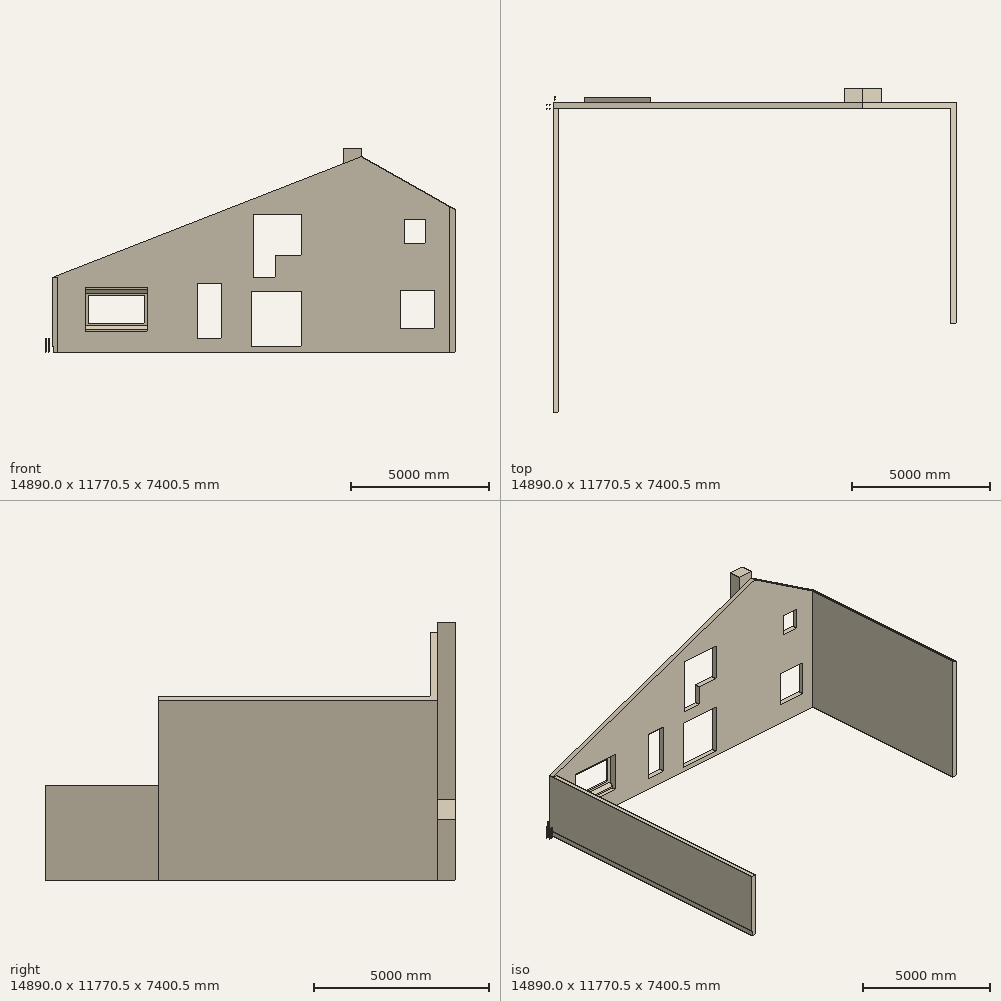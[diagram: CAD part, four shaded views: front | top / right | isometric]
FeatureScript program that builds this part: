
annotation { "Feature Type Name" : "Feature", "Feature Type Description" : "" }
export const myFeature = defineFeature(function(context is Context, id is Id, definition is map)
    precondition{}
    {
        {
            var Q0;
            Q0=qCreatedBy(makeId("Top.planeOp"),FACE);
            var sketch = newSketch(context, id + "F0", { "sketchPlane" : qUnion([Q0])});
            skLineSegment(sketch, "E0", {"start": v(-6130, 0) * mm, "end": v(8510, 0) * mm});
            skLineSegment(sketch, "E1", {"start": v(8510, 0) * mm, "end": v(8510, -8000.5) * mm});
            skLineSegment(sketch, "E2", {"start": v(-6130, 0) * mm, "end": v(-6130, -11250.5) * mm});
            skLineSegment(sketch, "E3.0", {"start": v(8310, -200) * mm, "end": v(8310, -8000.5) * mm});
            skLineSegment(sketch, "E3.1", {"start": v(-5930, -200) * mm, "end": v(8310, -200) * mm});
            skLineSegment(sketch, "E3.2", {"start": v(-5930, -200) * mm, "end": v(-5930, -11250.5) * mm});
            skLineSegment(sketch, "E4", {"start": v(-6130, -11250.5) * mm, "end": v(-5930, -11250.5) * mm});
            skLineSegment(sketch, "E5", {"start": v(8510, -8000.5) * mm, "end": v(8310, -8000.5) * mm});
            skSolve(sketch);
        }
        {
            var Q0;
            Q0 = qSketchRegion(id + "F0", true);
            extrude(context, id + "F1", {"entities" : qUnion([Q0]), "depth" : ((2374.5 - 100) - 50) * mm, "offsetDistance" : 25 * mm, "hasSecondDirection" : true, "secondDirectionOppositeDirection" : true, "secondDirectionDepth" : 490 * mm});
        }
        {
            var Q0;
            Q0=makeQuery(id+"F1.opExtrude","SWEPT_FACE",FACE,{"disambiguationData":[OSD([sQuery(id+"F0.wireOp",EDGE,"E0")])]});
            var sketch = newSketch(context, id + "F2", { "sketchPlane" : qUnion([Q0])});
            skLineSegment(sketch, "E6.bottom", {"start": v(0, 0) * mm, "end": v(850.5, 0) * mm});
            skLineSegment(sketch, "E6.top", {"start": v(0, 2000.5) * mm, "end": v(850.5, 2000.5) * mm});
            skLineSegment(sketch, "E6.left", {"start": v(0, 0) * mm, "end": v(0, 2000.5) * mm});
            skLineSegment(sketch, "E6.right", {"start": v(850.5, 0) * mm, "end": v(850.5, 2000.5) * mm});
            skLineSegment(sketch, "E7.bottom", {"start": v(-1100, -290) * mm, "end": v(-2920, -290) * mm});
            skLineSegment(sketch, "E7.top", {"start": v(-1100, 1710.5) * mm, "end": v(-2920, 1710.5) * mm});
            skLineSegment(sketch, "E7.left", {"start": v(-1100, -290) * mm, "end": v(-1100, 1710.5) * mm});
            skLineSegment(sketch, "E7.right", {"start": v(-2920, -290) * mm, "end": v(-2920, 1710.5) * mm});
            skLineSegment(sketch, "E8.bottom", {"start": v(-6530, 360) * mm, "end": v(-7750, 360) * mm});
            skLineSegment(sketch, "E8.top", {"start": v(-6530, 1760) * mm, "end": v(-7750, 1760) * mm});
            skLineSegment(sketch, "E8.left", {"start": v(-6530, 360) * mm, "end": v(-6530, 1760) * mm});
            skLineSegment(sketch, "E8.right", {"start": v(-7750, 360) * mm, "end": v(-7750, 1760) * mm});
            skLineSegment(sketch, "E9.bottom", {"start": v(-7419.5, 3475.5) * mm, "end": v(-6669.5, 3475.5) * mm});
            skLineSegment(sketch, "E9.top", {"start": v(-7419.5, 4325.5) * mm, "end": v(-6669.5, 4325.5) * mm});
            skLineSegment(sketch, "E9.left", {"start": v(-7419.5, 3475.5) * mm, "end": v(-7419.5, 4325.5) * mm});
            skLineSegment(sketch, "E9.right", {"start": v(-6669.5, 3475.5) * mm, "end": v(-6669.5, 4325.5) * mm});
            skSolve(sketch);
        }
        {
            var Q0;
            Q0=makeQuery(id+"F2.imprint","IMPRINT",FACE,{"disambiguationData":[TD([[makeQuery(id+"F2.imprint","IMPRINT",EDGE,{"derivedFrom":sQuery(id+"F2.wireOp",EDGE,"E6.bottom")}),1.0]])]});
            var Q1;
            Q1=makeQuery(id+"F2.imprint","IMPRINT",FACE,{"disambiguationData":[TD([[makeQuery(id+"F2.imprint","IMPRINT",EDGE,{"derivedFrom":sQuery(id+"F2.wireOp",EDGE,"E7.bottom")}),-1.0]])]});
            var Q2;
            Q2=makeQuery(id+"F2.imprint","IMPRINT",FACE,{"disambiguationData":[TD([[makeQuery(id+"F2.imprint","IMPRINT",EDGE,{"derivedFrom":sQuery(id+"F2.wireOp",EDGE,"E8.bottom")}),-1.0]])]});
            extrude(context, id + "F3", {"entities" : qUnion([Q0, Q1, Q2]), "operationType" : NewBodyOperationType.REMOVE, "endBound" : BoundingType.UP_TO_NEXT, "oppositeDirection" : true, "depth" : 25 * mm, "offsetDistance" : 25 * mm});
        }
        {
            var Q0;
            Q0=makeQuery(id+"F1.opExtrude","SWEPT_FACE",FACE,{"disambiguationData":[OSD([sQuery(id+"F0.wireOp",EDGE,"E0")])]});
            var sketch = newSketch(context, id + "F4", { "sketchPlane" : qUnion([Q0])});
            skLineSegment(sketch, "E10.bottom", {"start": v(2680, 260.5) * mm, "end": v(4920, 260.5) * mm});
            skLineSegment(sketch, "E10.top", {"start": v(2680, 1861) * mm, "end": v(4920, 1861) * mm});
            skLineSegment(sketch, "E10.left", {"start": v(2680, 260.5) * mm, "end": v(2680, 1861) * mm});
            skLineSegment(sketch, "E10.right", {"start": v(4920, 260.5) * mm, "end": v(4920, 1861) * mm});
            skSolve(sketch);
        }
        {
            var Q0;
            Q0 = qSketchRegion(id + "F4", true);
            extrude(context, id + "F5", {"entities" : qUnion([Q0]), "operationType" : NewBodyOperationType.REMOVE, "endBound" : BoundingType.UP_TO_NEXT, "oppositeDirection" : true, "depth" : 25 * mm, "offsetDistance" : 25 * mm});
        }
        {
            var Q0;
            Q0=makeQuery(id+"F5.boolean.opBoolean","COPY",FACE,{"derivedFrom":makeQuery(id+"F5.opExtrude","SWEPT_FACE",FACE,{"disambiguationData":[OSD([sQuery(id+"F4.wireOp",EDGE,"E10.left")])]})});
            var sketch = newSketch(context, id + "F6", { "sketchPlane" : qUnion([Q0])});
            skLineSegment(sketch, "E11", {"start": v(0, 1861) * mm, "end": v(-175, 1683.25) * mm});
            skLineSegment(sketch, "E12", {"start": v(-175, 1683.25) * mm, "end": v(-175, 438.25) * mm});
            skLineSegment(sketch, "E13", {"start": v(-175, 438.25) * mm, "end": v(0, 260.5) * mm});
            skLineSegment(sketch, "E14", {"start": v(-175, 1060.75) * mm, "end": v(0, 1060.75) * mm, "construction": true});
            skPoint(sketch, "E14.endSnap0", {"position": v(0, 1060.75) * mm});
            skLineSegment(sketch, "E15.0", {"start": v(-95, 471.02) * mm, "end": v(44.64, 329.19) * mm});
            skLineSegment(sketch, "E15.1", {"start": v(-95, 1650.48) * mm, "end": v(-95, 471.02) * mm});
            skLineSegment(sketch, "E15.2", {"start": v(44.64, 1792.31) * mm, "end": v(-95, 1650.48) * mm});
            skLineSegment(sketch, "E16", {"start": v(44.64, 1792.31) * mm, "end": v(44.64, 1861) * mm});
            skLineSegment(sketch, "E17", {"start": v(44.64, 1861) * mm, "end": v(0, 1861) * mm});
            skLineSegment(sketch, "E18", {"start": v(44.64, 329.19) * mm, "end": v(44.64, 260.5) * mm});
            skPoint(sketch, "E18.endSnap0", {"position": v(100, 260.5) * mm});
            skLineSegment(sketch, "E19", {"start": v(44.64, 260.5) * mm, "end": v(0, 260.5) * mm});
            skSolve(sketch);
        }
        {
            var Q0;
            Q0 = qSketchRegion(id + "F6", true);
            var Q1;
            Q1=makeQuery(id+"F5.boolean.opBoolean","COPY",FACE,{"derivedFrom":makeQuery(id+"F5.opExtrude","SWEPT_FACE",FACE,{"disambiguationData":[OSD([sQuery(id+"F4.wireOp",EDGE,"E10.right")])]})});
            extrude(context, id + "F7", {"entities" : qUnion([Q0]), "operationType" : NewBodyOperationType.ADD, "endBound" : BoundingType.UP_TO_SURFACE, "depth" : 25 * mm, "endBoundEntityFace" : qUnion([Q1]), "offsetDistance" : 25 * mm});
        }
        {
            var Q0;
            Q0=makeQuery(id+"F7.opExtrude","CAP_FACE",FACE,{"disambiguationData":[OSD([sQuery(id+"F6.wireOp",EDGE,"E11"),sQuery(id+"F6.wireOp",EDGE,"E12"),sQuery(id+"F6.wireOp",EDGE,"E13"),sQuery(id+"F6.wireOp",EDGE,"E15.0"),sQuery(id+"F6.wireOp",EDGE,"E15.1"),sQuery(id+"F6.wireOp",EDGE,"E15.2"),sQuery(id+"F6.wireOp",EDGE,"E16"),sQuery(id+"F6.wireOp",EDGE,"E17"),sQuery(id+"F6.wireOp",EDGE,"E18"),sQuery(id+"F6.wireOp",EDGE,"E19")])],"isStart":true});
            var sketch = newSketch(context, id + "F8", { "sketchPlane" : qUnion([Q0])});
            skLineSegment(sketch, "E20.0", {"start": v(175, 1683.25) * mm, "end": v(175, 438.25) * mm});
            skLineSegment(sketch, "E21.0", {"start": v(0, 1861) * mm, "end": v(175, 1683.25) * mm});
            skLineSegment(sketch, "E22.0", {"start": v(175, 438.25) * mm, "end": v(0, 260.5) * mm});
            skLineSegment(sketch, "E23", {"start": v(0, 260.5) * mm, "end": v(0, 1861) * mm});
            skSolve(sketch);
        }
        {
            var Q0;
            Q0 = qSketchRegion(id + "F8", true);
            extrude(context, id + "F9", {"entities" : qUnion([Q0]), "operationType" : NewBodyOperationType.ADD, "depth" : 80 * mm, "offsetDistance" : 25 * mm});
        }
        {
            var Q0;
            Q0=makeQuery(id+"F9.opExtrude","CAP_FACE",FACE,{"disambiguationData":[OSD([sQuery(id+"F8.wireOp",EDGE,"E20.0"),sQuery(id+"F8.wireOp",EDGE,"E21.0"),sQuery(id+"F8.wireOp",EDGE,"E22.0"),sQuery(id+"F8.wireOp",EDGE,"E23")])],"isStart":false});
            var Q1;
            Q1=makeQuery(id+"F5.boolean.opBoolean","COPY",FACE,{"derivedFrom":makeQuery(id+"F5.opExtrude","SWEPT_FACE",FACE,{"disambiguationData":[OSD([sQuery(id+"F4.wireOp",EDGE,"E10.right")])]})});
            var Q2;
            Q2=makeQuery(id+"F5.boolean.opBoolean","COPY",FACE,{"derivedFrom":makeQuery(id+"F5.opExtrude","SWEPT_FACE",FACE,{"disambiguationData":[OSD([sQuery(id+"F4.wireOp",EDGE,"E10.right")])]})});
            extrude(context, id + "F10", {"entities" : qUnion([Q0]), "operationType" : NewBodyOperationType.ADD, "endBound" : BoundingType.UP_TO_SURFACE, "oppositeDirection" : true, "depth" : 25 * mm, "endBoundEntityFace" : qUnion([Q1]), "hasOffset" : true, "offsetDistance" : 80 * mm, "offsetOppositeDirection" : true, "hasSecondDirection" : true, "secondDirectionBound" : SecondDirectionBoundingType.UP_TO_SURFACE, "secondDirectionOppositeDirection" : true, "secondDirectionDepth" : 80 * mm, "secondDirectionBoundEntityFace" : qUnion([Q2])});
        }
        {
            var Q0;
            {var subQ0=sQuery(id+"F8.wireOp",EDGE,"E20.0");Q0=makeQuery(id+"F10.boolean.opBoolean","MERGE",FACE,{"derivedFrom":[makeQuery(id+"F9.boolean.opBoolean","MERGE",FACE,{"derivedFrom":[makeQuery(id+"F7.opExtrude","SWEPT_FACE",FACE,{"disambiguationData":[OSD([sQuery(id+"F6.wireOp",EDGE,"E12")])]}),makeQuery(id+"F9.opExtrude","SWEPT_FACE",FACE,{"disambiguationData":[OSD([subQ0])]})]}),makeQuery(id+"F10.opExtrude","SWEPT_FACE",FACE,{"disambiguationData":[OSD([subQ0])]})]});}
            var sketch = newSketch(context, id + "F11", { "sketchPlane" : qUnion([Q0])});
            skLineSegment(sketch, "E24", {"start": v(3800, 1683.25) * mm, "end": v(3800, 438.25) * mm, "construction": true});
            skLineSegment(sketch, "E25.bottom", {"start": v(4800.25, 1561) * mm, "end": v(2799.75, 1561) * mm});
            skLineSegment(sketch, "E25.top", {"start": v(4800.25, 560.5) * mm, "end": v(2799.75, 560.5) * mm});
            skLineSegment(sketch, "E25.left", {"start": v(4800.25, 1561) * mm, "end": v(4800.25, 560.5) * mm});
            skLineSegment(sketch, "E25.right", {"start": v(2799.75, 1561) * mm, "end": v(2799.75, 560.5) * mm});
            skPoint(sketch, "E25.middle", {"position": v(3800, 1060.75) * mm});
            skSolve(sketch);
        }
        {
            var Q0;
            Q0 = qSketchRegion(id + "F11", true);
            extrude(context, id + "F12", {"entities" : qUnion([Q0]), "operationType" : NewBodyOperationType.REMOVE, "endBound" : BoundingType.UP_TO_NEXT, "oppositeDirection" : true, "depth" : 25 * mm, "offsetDistance" : 25 * mm});
        }
        {
            var Q0;
            Q0=makeQuery(id+"F1.opExtrude","SWEPT_FACE",FACE,{"disambiguationData":[OSD([sQuery(id+"F0.wireOp",EDGE,"E0")])]});
            var sketch = newSketch(context, id + "F13", { "sketchPlane" : qUnion([Q0])});
            skLineSegment(sketch, "E26", {"start": v(-5100.5, 6616.92) * mm, "end": v(6130, 2224.5) * mm});
            skLineSegment(sketch, "E27", {"start": v(6130, 2224.5) * mm, "end": v(-8510, 2224.5) * mm});
            skLineSegment(sketch, "E28", {"start": v(-8510, 2224.5) * mm, "end": v(-8510, 4687.5) * mm});
            skLineSegment(sketch, "E29", {"start": v(-8510, 4687.5) * mm, "end": v(-5100.5, 6616.92) * mm});
            skSolve(sketch);
        }
        {
            var Q0;
            Q0=makeQuery(id+"F13.imprint","IMPRINT",FACE,{"disambiguationData":[TD([[makeQuery(id+"F13.imprint","IMPRINT",EDGE,{"derivedFrom":sQuery(id+"F13.wireOp",EDGE,"E26")}),-1.0]])]});
            var Q1;
            Q1=makeQuery(id+"F1.opExtrude","SWEPT_FACE",FACE,{"disambiguationData":[OSD([sQuery(id+"F0.wireOp",EDGE,"E3.1")])]});
            extrude(context, id + "F14", {"entities" : qUnion([Q0]), "operationType" : NewBodyOperationType.ADD, "endBound" : BoundingType.UP_TO_SURFACE, "oppositeDirection" : true, "depth" : 25 * mm, "endBoundEntityFace" : qUnion([Q1]), "offsetDistance" : 25 * mm});
        }
        {
            var Q0;
            {var subQ0=sQuery(id+"F0.wireOp",EDGE,"E5");var subQ1=sQuery(id+"F0.wireOp",EDGE,"E3.1");var subQ2=sQuery(id+"F0.wireOp",EDGE,"E3.0");var subQ4=sQuery(id+"F0.wireOp",EDGE,"E1");Q0=makeQuery(id+"F14.boolean.opBoolean","SPLIT",FACE,{"disambiguationData":[TD([makeQuery(id+"F1.opExtrude","SWEPT_FACE",FACE,{"disambiguationData":[OSD([subQ4])]})])],"derivedFrom":makeQuery(id+"F1.opExtrude","CAP_FACE",FACE,{"disambiguationData":[OSD([sQuery(id+"F0.wireOp",EDGE,"E0"),subQ4,sQuery(id+"F0.wireOp",EDGE,"E2"),subQ2,subQ1,sQuery(id+"F0.wireOp",EDGE,"E3.2"),sQuery(id+"F0.wireOp",EDGE,"E4"),subQ0])],"isStart":false})});}
            var Q1;
            Q1=makeQuery(id+"F14.opExtrude","SWEPT_FACE",FACE,{"disambiguationData":[OSD([sQuery(id+"F13.wireOp",EDGE,"E29")])]});
            extrude(context, id + "F15", {"entities" : qUnion([Q0]), "operationType" : NewBodyOperationType.ADD, "endBound" : BoundingType.UP_TO_SURFACE, "depth" : 25 * mm, "endBoundEntityFace" : qUnion([Q1]), "offsetDistance" : 25 * mm});
        }
        {
            var Q0;
            Q0=makeQuery(id+"F2.imprint","IMPRINT",FACE,{"disambiguationData":[TD([[makeQuery(id+"F2.imprint","IMPRINT",EDGE,{"derivedFrom":sQuery(id+"F2.wireOp",EDGE,"E9.bottom")}),1.0]])]});
            extrude(context, id + "F16", {"entities" : qUnion([Q0]), "operationType" : NewBodyOperationType.REMOVE, "endBound" : BoundingType.UP_TO_NEXT, "oppositeDirection" : true, "depth" : 25 * mm, "offsetDistance" : 25 * mm});
        }
        {
            var Q0;
            Q0=makeQuery(id+"F14.boolean.opBoolean","MERGE",FACE,{"derivedFrom":[makeQuery(id+"F1.opExtrude","SWEPT_FACE",FACE,{"disambiguationData":[OSD([sQuery(id+"F0.wireOp",EDGE,"E0")])]}),makeQuery(id+"F14.opExtrude","CAP_FACE",FACE,{"disambiguationData":[OSD([sQuery(id+"F13.wireOp",EDGE,"E26"),sQuery(id+"F13.wireOp",EDGE,"E27"),sQuery(id+"F13.wireOp",EDGE,"E28"),sQuery(id+"F13.wireOp",EDGE,"E29")])],"isStart":true})]});
            var sketch = newSketch(context, id + "F17", { "sketchPlane" : qUnion([Q0])});
            skLineSegment(sketch, "E30", {"start": v(-2920, 3020.5) * mm, "end": v(-2920, 4501) * mm});
            skLineSegment(sketch, "E31", {"start": v(-2920, 4501) * mm, "end": v(-1189.5, 4501) * mm});
            skLineSegment(sketch, "E32", {"start": v(-1189.5, 4501) * mm, "end": v(-1189.5, 2220.5) * mm});
            skLineSegment(sketch, "E33", {"start": v(-1189.5, 2220.5) * mm, "end": v(-1990, 2220.5) * mm});
            skLineSegment(sketch, "E34", {"start": v(-1990, 2220.5) * mm, "end": v(-1990, 3020.5) * mm});
            skLineSegment(sketch, "E35", {"start": v(-1990, 3020.5) * mm, "end": v(-2920, 3020.5) * mm});
            skSolve(sketch);
        }
        {
            var Q0;
            Q0 = qSketchRegion(id + "F17", true);
            var Q1;
            Q1=makeQuery(id+"F14.boolean.opBoolean","MERGE",FACE,{"derivedFrom":[makeQuery(id+"F1.opExtrude","SWEPT_FACE",FACE,{"disambiguationData":[OSD([sQuery(id+"F0.wireOp",EDGE,"E3.1")])]}),makeQuery(id+"F14.opExtrude","CAP_FACE",FACE,{"disambiguationData":[OSD([sQuery(id+"F13.wireOp",EDGE,"E26"),sQuery(id+"F13.wireOp",EDGE,"E27"),sQuery(id+"F13.wireOp",EDGE,"E28"),sQuery(id+"F13.wireOp",EDGE,"E29")])],"isStart":false})]});
            extrude(context, id + "F18", {"entities" : qUnion([Q0]), "operationType" : NewBodyOperationType.REMOVE, "endBound" : BoundingType.UP_TO_SURFACE, "oppositeDirection" : true, "depth" : 25 * mm, "endBoundEntityFace" : qUnion([Q1]), "offsetDistance" : 25 * mm});
        }
        {
            var Q0;
            Q0=makeQuery(id+"F14.boolean.opBoolean","MERGE",FACE,{"derivedFrom":[makeQuery(id+"F1.opExtrude","SWEPT_FACE",FACE,{"disambiguationData":[OSD([sQuery(id+"F0.wireOp",EDGE,"E0")])]}),makeQuery(id+"F14.opExtrude","CAP_FACE",FACE,{"disambiguationData":[OSD([sQuery(id+"F13.wireOp",EDGE,"E26"),sQuery(id+"F13.wireOp",EDGE,"E27"),sQuery(id+"F13.wireOp",EDGE,"E28"),sQuery(id+"F13.wireOp",EDGE,"E29")])],"isStart":true})]});
            var sketch = newSketch(context, id + "F19", { "sketchPlane" : qUnion([Q0])});
            skLineSegment(sketch, "E36", {"start": v(-5100.5, 6910.5) * mm, "end": v(-5100.5, 1839.38) * mm});
            skLineSegment(sketch, "E37", {"start": v(-5100.5, 1839.38) * mm, "end": v(-5770, 1270.32) * mm});
            skLineSegment(sketch, "E38", {"start": v(-5770, 1270.32) * mm, "end": v(-5770, -490) * mm});
            skLineSegment(sketch, "E39", {"start": v(-5770, -490) * mm, "end": v(-4450, -490) * mm});
            skLineSegment(sketch, "E40", {"start": v(-4450, -490) * mm, "end": v(-4450, 6910.5) * mm});
            skLineSegment(sketch, "E41", {"start": v(-4450, 6910.5) * mm, "end": v(-5100.5, 6910.5) * mm});
            skSolve(sketch);
        }
        {
            var Q0;
            Q0 = qSketchRegion(id + "F19", true);
            extrude(context, id + "F20", {"entities" : qUnion([Q0]), "operationType" : NewBodyOperationType.ADD, "depth" : 520 * mm, "offsetDistance" : 25 * mm});
        }
        {
            var Q0;
            Q0=makeQuery(id+"F4.imprint","IMPRINT",FACE,{"disambiguationData":[TD([[makeQuery(id+"F4.imprint","IMPRINT",EDGE,{"derivedFrom":sQuery(id+"F4.wireOp",EDGE,"E10.bottom")}),-1.0]])]});
            var sketch = newSketch(context, id + "F21", { "sketchPlane" : qUnion([Q0])});
            skLineSegment(sketch, "E42", {"start": v(6130, -270) * mm, "end": v(-90, -270) * mm});
            skLineSegment(sketch, "E43", {"start": v(-90, -270) * mm, "end": v(-90, -450) * mm});
            skLineSegment(sketch, "E44", {"start": v(-90, -450) * mm, "end": v(-4450, -450) * mm});
            skLineSegment(sketch, "E45", {"start": v(-4450, -450) * mm, "end": v(-4450, -490) * mm});
            skLineSegment(sketch, "E46", {"start": v(6130, -490) * mm, "end": v(6130, -270) * mm});
            skLineSegment(sketch, "E47.0", {"start": v(6130, -490) * mm, "end": v(-4450, -490) * mm});
            skSolve(sketch);
        }
        {
            var Q0;
            Q0 = qSketchRegion(id + "F21", true);
            extrude(context, id + "F22", {"entities" : qUnion([Q0]), "operationType" : NewBodyOperationType.REMOVE, "oppositeDirection" : true, "depth" : 25 * mm, "offsetDistance" : 25 * mm});
        }
        {
            var Q0;
            Q0=makeQuery(id+"F1.opExtrude","SWEPT_FACE",FACE,{"disambiguationData":[OSD([sQuery(id+"F0.wireOp",EDGE,"E2")])]});
            var sketch = newSketch(context, id + "F23", { "sketchPlane" : qUnion([Q0])});
            skLineSegment(sketch, "E48.bottom", {"start": v(25, -270) * mm, "end": v(11250.5, -270) * mm});
            skLineSegment(sketch, "E48.top", {"start": v(25, -490) * mm, "end": v(11250.5, -490) * mm});
            skLineSegment(sketch, "E48.left", {"start": v(25, -270) * mm, "end": v(25, -490) * mm});
            skLineSegment(sketch, "E48.right", {"start": v(11250.5, -270) * mm, "end": v(11250.5, -490) * mm});
            skSolve(sketch);
        }
        {
            var Q0;
            Q0 = qSketchRegion(id + "F23", true);
            extrude(context, id + "F24", {"entities" : qUnion([Q0]), "operationType" : NewBodyOperationType.REMOVE, "oppositeDirection" : true, "depth" : 25 * mm, "offsetDistance" : 25 * mm});
        }
        {
            var Q0;
            Q0=makeQuery(id+"F20.boolean.opBoolean","MERGE",FACE,{"derivedFrom":[makeQuery(id+"F1.opExtrude","CAP_FACE",FACE,{"disambiguationData":[OSD([sQuery(id+"F0.wireOp",EDGE,"E0"),sQuery(id+"F0.wireOp",EDGE,"E1"),sQuery(id+"F0.wireOp",EDGE,"E2"),sQuery(id+"F0.wireOp",EDGE,"E3.0"),sQuery(id+"F0.wireOp",EDGE,"E3.1"),sQuery(id+"F0.wireOp",EDGE,"E3.2"),sQuery(id+"F0.wireOp",EDGE,"E4"),sQuery(id+"F0.wireOp",EDGE,"E5")])],"isStart":true}),makeQuery(id+"F20.opExtrude","SWEPT_FACE",FACE,{"disambiguationData":[OSD([sQuery(id+"F19.wireOp",EDGE,"E39")])]})]});
            var sketch = newSketch(context, id + "F25", { "sketchPlane" : qUnion([Q0])});
            skCircle(sketch, "E49", {"center": v(-6070, -190) * mm, "radius": 20 * mm});
            skCircle(sketch, "E50", {"center": v(-6070, -90) * mm, "radius": 20 * mm});
            skCircle(sketch, "E51", {"center": v(-6260, 70) * mm, "radius": 20 * mm});
            skCircle(sketch, "E52", {"center": v(-6260, 240) * mm, "radius": 20 * mm});
            skCircle(sketch, "E53", {"center": v(-6360, 240) * mm, "radius": 20 * mm});
            skCircle(sketch, "E54", {"center": v(-6360, 70) * mm, "radius": 20 * mm});
            skLineSegment(sketch, "E55", {"start": v(-6090, -90) * mm, "end": v(-6090, -190) * mm, "construction": true});
            skSolve(sketch);
        }
        {
            var Q0;
            Q0 = qSketchRegion(id + "F25", true);
            extrude(context, id + "F26", {"entities" : qUnion([Q0]), "oppositeDirection" : true, "depth" : 500 * mm, "offsetDistance" : 25 * mm});
        }
    });
